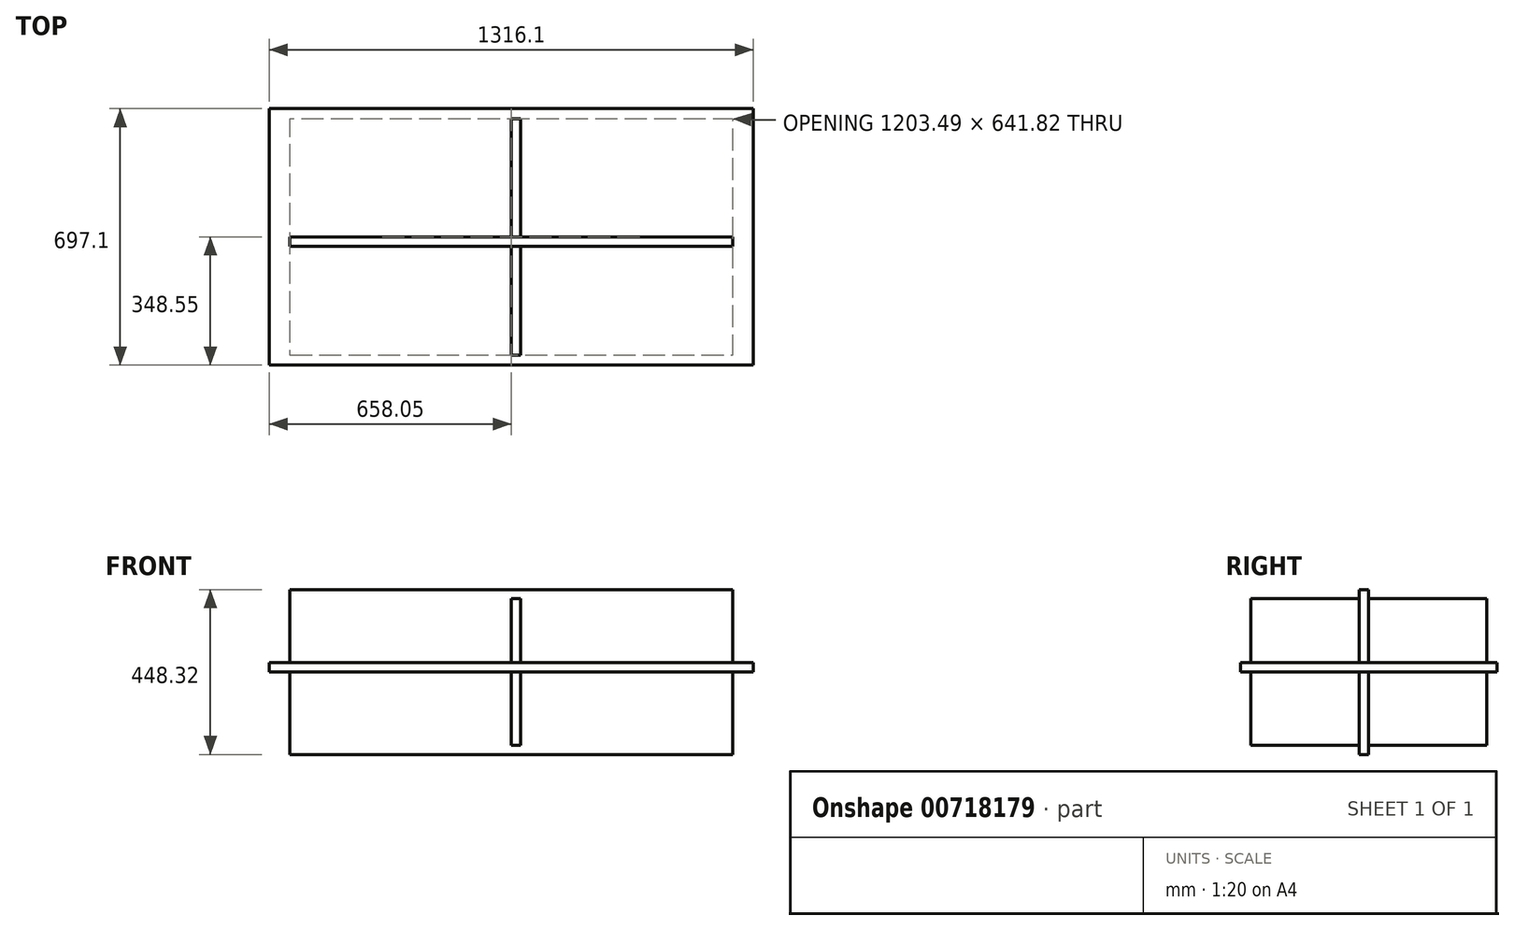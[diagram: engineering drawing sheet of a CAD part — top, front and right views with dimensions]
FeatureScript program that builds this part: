
annotation { "Feature Type Name" : "Feature", "Feature Type Description" : "" }
export const myFeature = defineFeature(function(context is Context, id is Id, definition is map)
    precondition{}
    {
        {
            var Q0;
            Q0=qCreatedBy(makeId("Front.planeOp"),FACE);
            var sketch = newSketch(context, id + "F0", { "sketchPlane" : qUnion([Q0])});
            skLineSegment(sketch, "E0.bottom", {"start": v(601.75, -224.16) * mm, "end": v(-601.75, -224.16) * mm});
            skLineSegment(sketch, "E0.top", {"start": v(601.75, 224.16) * mm, "end": v(-601.75, 224.16) * mm});
            skLineSegment(sketch, "E0.left", {"start": v(601.75, -224.16) * mm, "end": v(601.75, 224.16) * mm});
            skLineSegment(sketch, "E0.right", {"start": v(-601.75, -224.16) * mm, "end": v(-601.75, 224.16) * mm});
            skPoint(sketch, "E0.middle", {"position": v(0, 0) * mm});
            skSolve(sketch);
        }
        {
            var Q0;
            Q0 = qSketchRegion(id + "F0", true);
            extrude(context, id + "F1", {"entities" : qUnion([Q0]), "depth" : 25.4 * mm, "offsetDistance" : 25.4 * mm});
        }
        {
            var Q0;
            Q0=qCreatedBy(makeId("Top.planeOp"),FACE);
            var sketch = newSketch(context, id + "F2", { "sketchPlane" : qUnion([Q0])});
            skLineSegment(sketch, "E1.bottom", {"start": v(658.05, -348.55) * mm, "end": v(-658.05, -348.55) * mm});
            skLineSegment(sketch, "E1.top", {"start": v(658.05, 348.55) * mm, "end": v(-658.05, 348.55) * mm});
            skLineSegment(sketch, "E1.left", {"start": v(658.05, -348.55) * mm, "end": v(658.05, 348.55) * mm});
            skLineSegment(sketch, "E1.right", {"start": v(-658.05, -348.55) * mm, "end": v(-658.05, 348.55) * mm});
            skPoint(sketch, "E1.middle", {"position": v(0, 0) * mm});
            skSolve(sketch);
        }
        {
            var Q0;
            Q0 = qSketchRegion(id + "F2", true);
            extrude(context, id + "F3", {"entities" : qUnion([Q0]), "operationType" : NewBodyOperationType.ADD, "depth" : 25.4 * mm, "offsetDistance" : 25.4 * mm});
        }
        {
            var Q0;
            Q0=qCreatedBy(makeId("Right.planeOp"),FACE);
            var sketch = newSketch(context, id + "F4", { "sketchPlane" : qUnion([Q0])});
            skLineSegment(sketch, "E2.bottom", {"start": v(320.91, -199.37) * mm, "end": v(-320.91, -199.37) * mm});
            skLineSegment(sketch, "E2.top", {"start": v(320.91, 199.37) * mm, "end": v(-320.91, 199.37) * mm});
            skLineSegment(sketch, "E2.left", {"start": v(320.91, -199.37) * mm, "end": v(320.91, 199.37) * mm});
            skLineSegment(sketch, "E2.right", {"start": v(-320.91, -199.37) * mm, "end": v(-320.91, 199.37) * mm});
            skPoint(sketch, "E2.middle", {"position": v(0, 0) * mm});
            skSolve(sketch);
        }
        {
            var Q0;
            Q0 = qSketchRegion(id + "F4", true);
            extrude(context, id + "F5", {"entities" : qUnion([Q0]), "operationType" : NewBodyOperationType.ADD, "depth" : 25.4 * mm, "offsetDistance" : 25.4 * mm});
        }
    });
